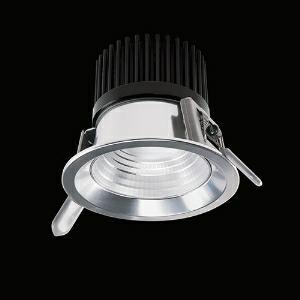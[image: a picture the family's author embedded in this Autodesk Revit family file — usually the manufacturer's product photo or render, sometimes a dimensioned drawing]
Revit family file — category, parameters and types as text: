
# Revit family: spectral_myral_myral_3500-830-s-dali
name_source: partatom
category: Lighting Fixtures
revit_build: Autodesk Revit 2016 (Build: 20150220_1215(x64)
units: mm (PartAtom-declared; Revit-internal decimal feet)

## family parameters
Cut with Voids When Loaded = No
Host = Face
Light Source = No
Part Type = Normal
Room Calculation Point = No
Round Connector Dimension = Use Diameter
Shared = No

## types (1)
- SPECTRAL MYRAL (1 x )
    Apparent Load = 0 VA
    Approval mark = CE
    CIE Flux Codes = 85 100 100 100 100
    Control Gear = Electronic transformer
    Default Elevation = 1800 mm
    Description = SPG0330174
MYRAL recessed spot

Design:
    Height = 0 mm  [stored 0 ft]
    Lamp = 1 x
    Lamp count = 1
    Length = 120 mm
    Luminous efficacy = 0 lm/W
    Manufacturer = Ridi
    ModVariant = No
    Model = MYRAL 3500-830-S-DALI
    Mounting Place = Ceiling
    Mounting Type = Recessed
    Number of Poles = 1
    OnlyDefault = Yes
    Power Factor = 1
    Product Name = SPECTRAL MYRAL
    Product group = Downlight recessed
    ProductGroupID = 400
    Protection Class = Protection class
    Protection Degree = IP 20
    RlxData = <blob elided: 38921 chars, md5=bc4016d1>
    Socket = socket
    Standby Power = 0 W
    System Light Flux = 0 lm
    System Power = 0 W
    Type Image = myral_04.jpg
    URL = http://reluxnet.relux.com
    VarID = ---
    Voltage = 0 V
    Weight = 0.00 kg
    Width = 0 mm  [stored 0 ft]

note: [stored X ft] marks values corroborated as IEEE doubles in the binary element streams (Revit-internal decimal feet)

## geometry (parser evidence)
native form markers: Sweep x7
no freeform markers — native parametric forms only
